FCSTD DOCUMENT  (FreeCAD 0.17R11939 (Git))
Label: bpt_motor_locknut_assy
License: All rights reserved
LicenseURL: http://en.wikipedia.org/wiki/All_rights_reserved
objects: Sketcher::SketchObject×2
note: 2 computed .brp shape members not serialized (recipe doc carries the construction recipe); baked Part::Feature solids carry a one-line shape summary decoded from their .brp

FEATURE [Sketcher::SketchObject] Sketch  label="handle"
  sketch-geometry (18):
    g0: LineSegment StartX=0 StartY=2.5 StartZ=0 EndX=5.2 EndY=2.5 EndZ=0
    g1: LineSegment StartX=5.2 StartY=2.5 StartZ=0 EndX=5.2 EndY=4.7625 EndZ=0
    g2: LineSegment StartX=5.2 StartY=4.7625 StartZ=0 EndX=9.7 EndY=4.7625 EndZ=0
    g3: LineSegment StartX=9.7 StartY=4.7625 StartZ=0 EndX=35.7 EndY=3 EndZ=0
    g4: LineSegment StartX=35.7 StartY=3 StartZ=0 EndX=35.7 EndY=4.7625 EndZ=0
    g5: LineSegment StartX=35.7 StartY=4.7625 StartZ=0 EndX=39.2 EndY=4.7625 EndZ=0
    g6: LineSegment StartX=39.2 StartY=4.7625 StartZ=0 EndX=39.2 EndY=2.5 EndZ=0
    g7: LineSegment StartX=39.2 StartY=2.5 StartZ=0 EndX=46.7 EndY=2.5 EndZ=0
    g8: LineSegment StartX=0 StartY=-2.5 StartZ=0 EndX=5.2 EndY=-2.5 EndZ=0
    g9: LineSegment StartX=5.2 StartY=-2.5 StartZ=0 EndX=5.2 EndY=-4.7625 EndZ=0
    g10: LineSegment StartX=5.2 StartY=-4.7625 StartZ=0 EndX=9.7 EndY=-4.7625 EndZ=0
    g11: LineSegment StartX=9.7 StartY=-4.7625 StartZ=0 EndX=35.7 EndY=-3 EndZ=0
    g12: LineSegment StartX=35.7 StartY=-3 StartZ=0 EndX=35.7 EndY=-4.7625 EndZ=0
    g13: LineSegment StartX=35.7 StartY=-4.7625 StartZ=0 EndX=39.2 EndY=-4.7625 EndZ=0
    g14: LineSegment StartX=39.2 StartY=-4.7625 StartZ=0 EndX=39.2 EndY=-2.5 EndZ=0
    g15: LineSegment StartX=39.2 StartY=-2.5 StartZ=0 EndX=46.7 EndY=-2.5 EndZ=0
    g16: LineSegment StartX=0 StartY=2.5 StartZ=0 EndX=0 EndY=-2.5 EndZ=0
    g17: LineSegment StartX=46.7 StartY=-2.5 StartZ=0 EndX=46.7 EndY=2.5 EndZ=0
  constraints (55):
    c: Horizontal(g0)
    c: Coincident(g0,g1)
    c: Vertical(g1)
    c: PointOnObject(g0,g-2)
    c: Coincident(g2,g1)
    c: Horizontal(g2)
    c: Coincident(g3,g2)
    c: Coincident(g4,g3)
    c: Vertical(g4)
    c: Coincident(g5,g4)
    c: Horizontal(g5)
    c: Coincident(g6,g5)
    c: Vertical(g6)
    c: Coincident(g7,g6)
    c: Horizontal(g7)
    c: Horizontal(g8)
    c: Coincident(g8,g9)
    c: Vertical(g9)
    c: Coincident(g10,g9)
    c: Horizontal(g10)
    c: Coincident(g11,g10)
    c: Coincident(g12,g11)
    c: Vertical(g12)
    c: Coincident(g13,g12)
    c: Horizontal(g13)
    c: Coincident(g14,g13)
    c: Vertical(g14)
    c: Coincident(g15,g14)
    c: Horizontal(g15)
    c: Coincident(g16,g0)
    c: Coincident(g16,g8)
    c: PointOnObject(g8,g-2)
    c: Coincident(g17,g15)
    c: Coincident(g17,g7)
    c: Vertical(g17)
    c: Symmetric(g6,g14,g-1)
    c: Symmetric(g3,g11,g-1)
    c: Symmetric(g0,g8,g-1)
    c: Equal(g1,g9)
    c: Equal(g4,g12)
    c: Equal(g10,g2)
    c: Distance(g5) = 3.5
    c: Distance(g16) = 5
    c: Distance(g17) = 5
    c: Distance(g1,g9) = 9.525
    c: Distance(g3,g11) = 6
    c: DistanceX(g2,g4) = 26
    c: Distance(g7) = 7.5
    c: Distance(g0) = 5.2
    c: Distance(g2) = 4.5
    c: DistanceY(g2,g4) = 0
    c: Angle(g3,g-1) = 0.0676849
    c: DistanceX(g8,g15) = 46.7
    c: DistanceX(g8,g12) = 35.7
    c: DistanceX(g9,g13) = 34
FEATURE [Sketcher::SketchObject] Sketch001  label="nut"
  MapMode = 2
  Support = -> [Sketch]
  sketch-geometry (11):
    g0: Circle CenterX=0 CenterY=0 CenterZ=0 NormalX=0 NormalY=0 NormalZ=1 Radius=4.42
    g1: Circle [constr] CenterX=0 CenterY=0 CenterZ=0 NormalX=0 NormalY=0 NormalZ=1 Radius=4.7625
    g2: ArcOfCircle CenterX=0 CenterY=0 CenterZ=0 NormalX=0 NormalY=0 NormalZ=1 Radius=12.7 StartAngle=0.320415 EndAngle=5.96277
    g3: LineSegment StartX=12.0536 StartY=-4 StartZ=0 EndX=12.0536 EndY=-2.1 EndZ=0
    g4: LineSegment StartX=12.0536 StartY=2.1 StartZ=0 EndX=5.2625 EndY=2.1 EndZ=0
    g5: LineSegment StartX=5.2625 StartY=2.1 StartZ=0 EndX=5.2625 EndY=-2.1 EndZ=0
    g6: LineSegment StartX=5.2625 StartY=-2.1 StartZ=0 EndX=12.0536 EndY=-2.1 EndZ=0
    g7: LineSegment StartX=12.0536 StartY=2.1 StartZ=0 EndX=12.0536 EndY=4 EndZ=0
    g8: LineSegment [constr] StartX=4.7625 StartY=0 StartZ=0 EndX=5.2625 EndY=0 EndZ=0
    g9: LineSegment StartX=5.2625 StartY=0 StartZ=0 EndX=6.24175 EndY=2.1 EndZ=0
    g10: LineSegment StartX=5.2625 StartY=0 StartZ=0 EndX=6.24175 EndY=-2.1 EndZ=0
  constraints (33):
    c: Coincident(g0,g-1)
    c: Radius(g0) = 4.42
    c: Coincident(g1,g-1)
    c: Radius(g1) = 4.7625
    c: Coincident(g2,g-1)
    c: Coincident(g3,g2)
    c: Coincident(g7,g2)
    c: Vertical(g3)
    c: Symmetric(g2,g2,g-1)
    c: Radius(g2) = 12.7
    c: Coincident(g5,g4)
    c: Vertical(g5)
    c: Coincident(g6,g5)
    c: Horizontal(g6)
    c: Horizontal(g4)
    c: Coincident(g3,g6)
    c: Coincident(g7,g4)
    c: Tangent(g3,g7)
    c: Symmetric(g4,g3,g-1)
    c: Distance(g4,g3) = 4.2
    c: Distance(g2,g2) = 8
    c: PointOnObject(g8,g5)
    c: Horizontal(g8)
    c: PointOnObject(g8,g1)
    c: PointOnObject(g8,g-1)
    c: Distance(g8) = 0.5
    c: Coincident(g9,g8)
    c: PointOnObject(g9,g4)
    c: Coincident(g10,g8)
    c: PointOnObject(g10,g6)
    c: Symmetric(g10,g9,g-1)
    c: Angle(g10,g9) = 2.26893
    c: DistanceX(g9,g4) = 5.81188
